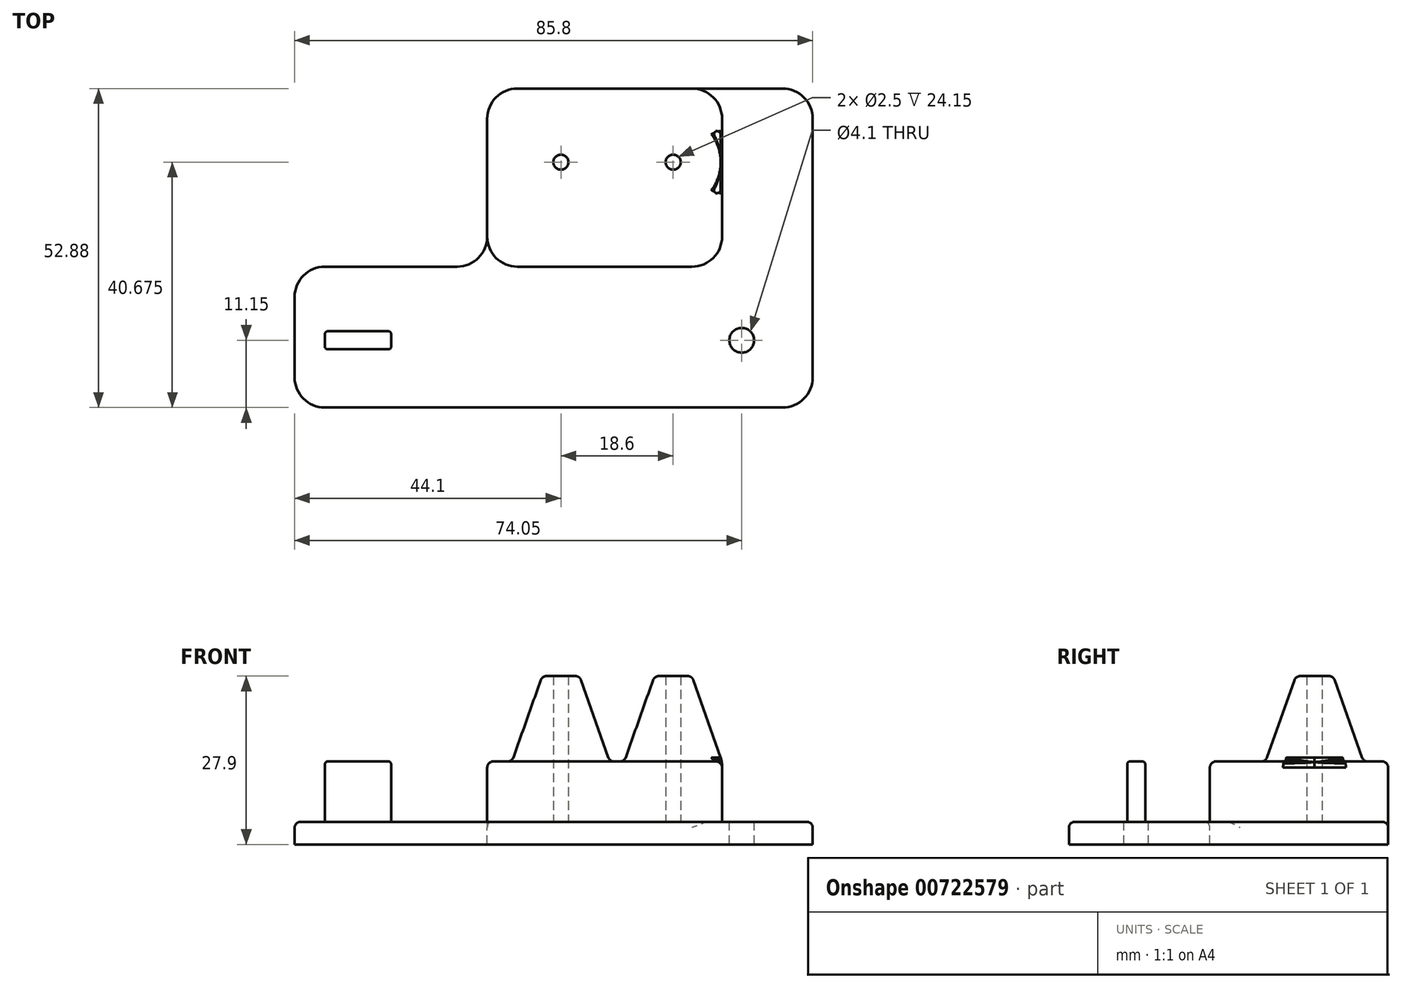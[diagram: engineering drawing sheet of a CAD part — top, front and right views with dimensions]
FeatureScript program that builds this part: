
annotation { "Feature Type Name" : "Feature", "Feature Type Description" : "" }
export const myFeature = defineFeature(function(context is Context, id is Id, definition is map)
    precondition{}
    {
        {
            var Q0;
            Q0=qCreatedBy(makeId("Top.planeOp"),FACE);
            var sketch = newSketch(context, id + "F0", { "sketchPlane" : qUnion([Q0])});
            skCircle(sketch, "E0", {"center": v(0, 0) * mm, "radius": 2.05 * mm});
            skLineSegment(sketch, "E1", {"start": v(2.05, 0) * mm, "end": v(40.45, 0) * mm, "construction": true});
            skLineSegment(sketch, "E2", {"start": v(40.45, 50) * mm, "end": v(40.45, 0) * mm, "construction": true});
            skCircle(sketch, "E3", {"center": v(-29.95, 29.52) * mm, "radius": 3.1 * mm});
            skCircle(sketch, "E4", {"center": v(-11.35, 29.52) * mm, "radius": 3.1 * mm});
            skLineSegment(sketch, "E5", {"start": v(-33.05, 30) * mm, "end": v(-33.05, 0) * mm, "construction": true});
            skLineSegment(sketch, "E6", {"start": v(-14.45, 30) * mm, "end": v(-14.45, 0) * mm, "construction": true});
            skLineSegment(sketch, "E7", {"start": v(-4.95, 0) * mm, "end": v(-4.95, 30) * mm, "construction": true});
            skLineSegment(sketch, "E8", {"start": v(-3.25, 41.72) * mm, "end": v(-3.25, 12.2) * mm});
            skLineSegment(sketch, "E9", {"start": v(0, -11.15) * mm, "end": v(-33.05, -11.15) * mm, "construction": true});
            skLineSegment(sketch, "E10", {"start": v(-29.95, 29.52) * mm, "end": v(-11.35, 29.52) * mm, "construction": true});
            skLineSegment(sketch, "E11", {"start": v(-29.95, 30.4) * mm, "end": v(-11.35, 30.4) * mm, "construction": true});
            skLineSegment(sketch, "E12", {"start": v(-3.25, 12.2) * mm, "end": v(-42.15, 12.2) * mm});
            skLineSegment(sketch, "E13", {"start": v(-42.15, 12.2) * mm, "end": v(-42.15, 41.72) * mm});
            skLineSegment(sketch, "E14", {"start": v(-42.15, 41.72) * mm, "end": v(-3.25, 41.72) * mm});
            skLineSegment(sketch, "E15", {"start": v(-3.25, 41.72) * mm, "end": v(11.75, 41.72) * mm});
            skLineSegment(sketch, "E16", {"start": v(11.75, 41.72) * mm, "end": v(11.75, -11.15) * mm});
            skLineSegment(sketch, "E17", {"start": v(11.75, -11.15) * mm, "end": v(-42.15, -11.15) * mm});
            skLineSegment(sketch, "E18", {"start": v(-42.15, -11.15) * mm, "end": v(-42.15, 12.2) * mm});
            skCircle(sketch, "E19", {"center": v(-11.35, 29.52) * mm, "radius": 1.25 * mm});
            skCircle(sketch, "E20", {"center": v(-29.95, 29.52) * mm, "radius": 1.25 * mm});
            skLineSegment(sketch, "E21.bottom", {"start": v(-69.05, 1.5) * mm, "end": v(-58.05, 1.5) * mm});
            skLineSegment(sketch, "E21.top", {"start": v(-69.05, -1.5) * mm, "end": v(-58.05, -1.5) * mm});
            skLineSegment(sketch, "E21.left", {"start": v(-69.05, 1.5) * mm, "end": v(-69.05, -1.5) * mm});
            skLineSegment(sketch, "E21.right", {"start": v(-58.05, 1.5) * mm, "end": v(-58.05, -1.5) * mm});
            skLineSegment(sketch, "E22", {"start": v(-69.05, -1.5) * mm, "end": v(-58.05, 1.5) * mm, "construction": true});
            skLineSegment(sketch, "E23", {"start": v(-63.55, 0) * mm, "end": v(-14.45, 0) * mm, "construction": true});
            skLineSegment(sketch, "E24", {"start": v(-42.15, 12.2) * mm, "end": v(-74.05, 12.2) * mm});
            skLineSegment(sketch, "E25", {"start": v(-74.05, 12.2) * mm, "end": v(-74.05, -11.15) * mm});
            skLineSegment(sketch, "E26", {"start": v(-74.05, -11.15) * mm, "end": v(-42.15, -11.15) * mm});
            skSolve(sketch);
        }
        {
            var Q0;
            Q0=makeQuery(id+"F0.imprint","IMPRINT",FACE,{"disambiguationData":[TD([[makeQuery(id+"F0.imprint","IMPRINT",EDGE,{"derivedFrom":sQuery(id+"F0.wireOp",EDGE,"E3")}),1.0]])]});
            var Q1;
            Q1=makeQuery(id+"F0.imprint","IMPRINT",FACE,{"disambiguationData":[TD([[makeQuery(id+"F0.imprint","IMPRINT",EDGE,{"derivedFrom":sQuery(id+"F0.wireOp",EDGE,"E4")}),1.0]])]});
            var Q2;
            Q2=makeQuery(id+"F0.imprint","IMPRINT",FACE,{"disambiguationData":[TD([[makeQuery(id+"F0.imprint","IMPRINT",EDGE,{"derivedFrom":sQuery(id+"F0.wireOp",EDGE,"E3")}),-1.0]])]});
            var Q3;
            Q3=makeQuery(id+"F0.imprint","IMPRINT",FACE,{"disambiguationData":[TD([[makeQuery(id+"F0.imprint","IMPRINT",EDGE,{"derivedFrom":sQuery(id+"F0.wireOp",EDGE,"E0")}),-1.0]])]});
            var Q4;
            Q4=makeQuery(id+"F0.imprint","IMPRINT",FACE,{"disambiguationData":[TD([[makeQuery(id+"F0.imprint","IMPRINT",EDGE,{"derivedFrom":sQuery(id+"F0.wireOp",EDGE,"E20")}),1.0]])]});
            var Q5;
            Q5=makeQuery(id+"F0.imprint","IMPRINT",FACE,{"disambiguationData":[TD([[makeQuery(id+"F0.imprint","IMPRINT",EDGE,{"derivedFrom":sQuery(id+"F0.wireOp",EDGE,"E19")}),1.0]])]});
            var Q6;
            Q6=makeQuery(id+"F0.imprint","IMPRINT",FACE,{"disambiguationData":[TD([[makeQuery(id+"F0.imprint","IMPRINT",EDGE,{"derivedFrom":sQuery(id+"F0.wireOp",EDGE,"E18")}),1.0]])]});
            var Q7;
            Q7=makeQuery(id+"F0.imprint","IMPRINT",FACE,{"disambiguationData":[TD([[makeQuery(id+"F0.imprint","IMPRINT",EDGE,{"derivedFrom":sQuery(id+"F0.wireOp",EDGE,"E21.bottom")}),-1.0]])]});
            extrude(context, id + "F1", {"entities" : qUnion([Q0, Q1, Q2, Q3, Q4, Q5, Q6, Q7]), "oppositeDirection" : true, "depth" : 3.75 * mm, "offsetDistance" : 25 * mm});
        }
        {
            var Q0;
            Q0=makeQuery(id+"F0.imprint","IMPRINT",FACE,{"disambiguationData":[TD([[makeQuery(id+"F0.imprint","IMPRINT",EDGE,{"derivedFrom":sQuery(id+"F0.wireOp",EDGE,"E3")}),1.0]])]});
            var Q1;
            Q1=makeQuery(id+"F0.imprint","IMPRINT",FACE,{"disambiguationData":[TD([[makeQuery(id+"F0.imprint","IMPRINT",EDGE,{"derivedFrom":sQuery(id+"F0.wireOp",EDGE,"E4")}),1.0]])]});
            var Q2;
            Q2=makeQuery(id+"F0.imprint","IMPRINT",FACE,{"disambiguationData":[TD([[makeQuery(id+"F0.imprint","IMPRINT",EDGE,{"derivedFrom":sQuery(id+"F0.wireOp",EDGE,"E3")}),-1.0]])]});
            var Q3;
            Q3=makeQuery(id+"F0.imprint","IMPRINT",FACE,{"disambiguationData":[TD([[makeQuery(id+"F0.imprint","IMPRINT",EDGE,{"derivedFrom":sQuery(id+"F0.wireOp",EDGE,"E21.bottom")}),-1.0]])]});
            extrude(context, id + "F2", {"entities" : qUnion([Q0, Q1, Q2, Q3]), "operationType" : NewBodyOperationType.ADD, "depth" : 10 * mm, "offsetDistance" : 25 * mm});
        }
        {
            var Q0;
            Q0=makeQuery(id+"F0.imprint","IMPRINT",FACE,{"disambiguationData":[TD([[makeQuery(id+"F0.imprint","IMPRINT",EDGE,{"derivedFrom":sQuery(id+"F0.wireOp",EDGE,"E4")}),1.0]])]});
            var Q1;
            Q1=makeQuery(id+"F0.imprint","IMPRINT",FACE,{"disambiguationData":[TD([[makeQuery(id+"F0.imprint","IMPRINT",EDGE,{"derivedFrom":sQuery(id+"F0.wireOp",EDGE,"E3")}),1.0]])]});
            extrude(context, id + "F3", {"entities" : qUnion([Q0, Q1]), "operationType" : NewBodyOperationType.ADD, "depth" : 24.15 * mm, "offsetDistance" : 25 * mm});
        }
        {
            var Q0;
            Q0=makeQuery(id+"F3.boolean.opBoolean","INTERSECT",EDGE,{"derivedFrom":[makeQuery(id+"F2.opExtrude","CAP_FACE",FACE,{"disambiguationData":[OSD([sQuery(id+"F0.wireOp",EDGE,"E8"),sQuery(id+"F0.wireOp",EDGE,"E12"),sQuery(id+"F0.wireOp",EDGE,"E13"),sQuery(id+"F0.wireOp",EDGE,"E14"),sQuery(id+"F0.wireOp",EDGE,"E19"),sQuery(id+"F0.wireOp",EDGE,"E20")])],"isStart":false}),makeQuery(id+"F3.opExtrude","SWEPT_FACE",FACE,{"disambiguationData":[OSD([sQuery(id+"F0.wireOp",EDGE,"E3")])]})]});
            var Q1;
            Q1=makeQuery(id+"F3.boolean.opBoolean","INTERSECT",EDGE,{"derivedFrom":[makeQuery(id+"F2.opExtrude","CAP_FACE",FACE,{"disambiguationData":[OSD([sQuery(id+"F0.wireOp",EDGE,"E8"),sQuery(id+"F0.wireOp",EDGE,"E12"),sQuery(id+"F0.wireOp",EDGE,"E13"),sQuery(id+"F0.wireOp",EDGE,"E14"),sQuery(id+"F0.wireOp",EDGE,"E19"),sQuery(id+"F0.wireOp",EDGE,"E20")])],"isStart":false}),makeQuery(id+"F3.opExtrude","SWEPT_FACE",FACE,{"disambiguationData":[OSD([sQuery(id+"F0.wireOp",EDGE,"E4")])]})]});
            chamfer(context, id + "F4", {"entities" : qUnion([Q0, Q1]), "chamferType" : ChamferType.TWO_OFFSETS, "width1" : 5 * mm, "oppositeDirection" : false, "width2" : 14.15 * mm, "tangentPropagation" : true});
        }
        {
            var Q0;
            Q0=makeQuery(id+"F1.opExtrude","SWEPT_EDGE",EDGE,{"disambiguationData":[OSD([sQuery(id+"F0.wireOp",EDGE,"E16"),sQuery(id+"F0.wireOp",EDGE,"E17")])]});
            var Q1;
            Q1=makeQuery(id+"F1.opExtrude","SWEPT_EDGE",EDGE,{"disambiguationData":[OSD([sQuery(id+"F0.wireOp",EDGE,"E17"),sQuery(id+"F0.wireOp",EDGE,"E18")])]});
            var Q2;
            Q2=makeQuery(id+"F1.opExtrude","SWEPT_EDGE",EDGE,{"disambiguationData":[OSD([sQuery(id+"F0.wireOp",EDGE,"E15"),sQuery(id+"F0.wireOp",EDGE,"E16")])]});
            var Q3;
            Q3=makeQuery(id+"F2.opExtrude","SWEPT_EDGE",EDGE,{"disambiguationData":[OSD([sQuery(id+"F0.wireOp",EDGE,"E8"),sQuery(id+"F0.wireOp",EDGE,"E12")])]});
            var Q4;
            Q4=makeQuery(id+"F2.opExtrude","SWEPT_EDGE",EDGE,{"disambiguationData":[OSD([sQuery(id+"F0.wireOp",EDGE,"E12"),sQuery(id+"F0.wireOp",EDGE,"E13"),sQuery(id+"F0.wireOp",EDGE,"E18")])]});
            var Q5;
            {var subQ0=sQuery(id+"F0.wireOp",EDGE,"E14");var subQ1=sQuery(id+"F0.wireOp",EDGE,"E13");Q5=makeQuery(id+"F2.boolean.opBoolean","MERGE",EDGE,{"derivedFrom":[makeQuery(id+"F1.opExtrude","SWEPT_EDGE",EDGE,{"disambiguationData":[OSD([subQ1,subQ0])]}),makeQuery(id+"F2.opExtrude","SWEPT_EDGE",EDGE,{"disambiguationData":[OSD([subQ1,subQ0])]})]});}
            var Q6;
            Q6=makeQuery(id+"F2.opExtrude","SWEPT_EDGE",EDGE,{"disambiguationData":[OSD([sQuery(id+"F0.wireOp",EDGE,"E8"),sQuery(id+"F0.wireOp",EDGE,"E14"),sQuery(id+"F0.wireOp",EDGE,"E15")])]});
            var Q7;
            Q7=makeQuery(id+"F1.opExtrude","SWEPT_EDGE",EDGE,{"disambiguationData":[OSD([sQuery(id+"F0.wireOp",EDGE,"E24"),sQuery(id+"F0.wireOp",EDGE,"E25")])]});
            var Q8;
            Q8=makeQuery(id+"F1.opExtrude","SWEPT_EDGE",EDGE,{"disambiguationData":[OSD([sQuery(id+"F0.wireOp",EDGE,"E25"),sQuery(id+"F0.wireOp",EDGE,"E26")])]});
            fillet(context, id + "F5", {"entities" : qUnion([Q0, Q1, Q2, Q3, Q4, Q5, Q6, Q7, Q8]), "radius" : 5 * mm, "tangentPropagation" : true, "allowEdgeOverflow" : false});
        }
        {
            var Q0;
            Q0=makeQuery(id+"F1.opExtrude","SWEPT_EDGE",EDGE,{"disambiguationData":[OSD([sQuery(id+"F0.wireOp",EDGE,"E12"),sQuery(id+"F0.wireOp",EDGE,"E13"),sQuery(id+"F0.wireOp",EDGE,"E18"),sQuery(id+"F0.wireOp",EDGE,"E24")])]});
            fillet(context, id + "F6", {"entities" : qUnion([Q0]), "radius" : 5 * mm, "tangentPropagation" : true, "allowEdgeOverflow" : false});
        }
        {
            var Q0;
            Q0=makeQuery(id+"F2.opExtrude","CAP_FACE",FACE,{"disambiguationData":[OSD([sQuery(id+"F0.wireOp",EDGE,"E21.bottom"),sQuery(id+"F0.wireOp",EDGE,"E21.top"),sQuery(id+"F0.wireOp",EDGE,"E21.left"),sQuery(id+"F0.wireOp",EDGE,"E21.right")])],"isStart":false});
            var Q1;
            Q1=makeQuery(id+"F2.opExtrude","SWEPT_EDGE",EDGE,{"disambiguationData":[OSD([sQuery(id+"F0.wireOp",EDGE,"E21.bottom"),sQuery(id+"F0.wireOp",EDGE,"E21.left")])]});
            var Q2;
            Q2=makeQuery(id+"F2.opExtrude","SWEPT_EDGE",EDGE,{"disambiguationData":[OSD([sQuery(id+"F0.wireOp",EDGE,"E21.top"),sQuery(id+"F0.wireOp",EDGE,"E21.left")])]});
            var Q3;
            Q3=makeQuery(id+"F2.opExtrude","SWEPT_EDGE",EDGE,{"disambiguationData":[OSD([sQuery(id+"F0.wireOp",EDGE,"E21.bottom"),sQuery(id+"F0.wireOp",EDGE,"E21.right")])]});
            var Q4;
            Q4=makeQuery(id+"F2.opExtrude","SWEPT_EDGE",EDGE,{"disambiguationData":[OSD([sQuery(id+"F0.wireOp",EDGE,"E21.top"),sQuery(id+"F0.wireOp",EDGE,"E21.right")])]});
            fillet(context, id + "F7", {"entities" : qUnion([Q0, Q1, Q2, Q3, Q4]), "radius" : 0.5 * mm, "tangentPropagation" : true, "allowEdgeOverflow" : false});
        }
        {
            var Q0;
            Q0=makeQuery(id+"F2.opExtrude","CAP_FACE",FACE,{"disambiguationData":[OSD([sQuery(id+"F0.wireOp",EDGE,"E8"),sQuery(id+"F0.wireOp",EDGE,"E12"),sQuery(id+"F0.wireOp",EDGE,"E13"),sQuery(id+"F0.wireOp",EDGE,"E14"),sQuery(id+"F0.wireOp",EDGE,"E19"),sQuery(id+"F0.wireOp",EDGE,"E20")])],"isStart":false});
            var Q1;
            {var subQ0=sQuery(id+"F0.wireOp",EDGE,"E20");var subQ1=sQuery(id+"F0.wireOp",EDGE,"E3");Q1=makeQuery(id+"F4.opChamfer","BLEND_EDGE",EDGE,{"blendedFrom":[makeQuery(id+"F3.boolean.opBoolean","INTERSECT",EDGE,{"derivedFrom":[makeQuery(id+"F2.opExtrude","CAP_FACE",FACE,{"disambiguationData":[OSD([sQuery(id+"F0.wireOp",EDGE,"E8"),sQuery(id+"F0.wireOp",EDGE,"E12"),sQuery(id+"F0.wireOp",EDGE,"E13"),sQuery(id+"F0.wireOp",EDGE,"E14"),sQuery(id+"F0.wireOp",EDGE,"E19"),subQ0])],"isStart":false}),makeQuery(id+"F3.opExtrude","SWEPT_FACE",FACE,{"disambiguationData":[OSD([subQ1])]})]}),makeQuery(id+"F3.opExtrude","CAP_FACE",FACE,{"disambiguationData":[OSD([subQ1,subQ0])],"isStart":false})],"blendedInto":[makeQuery(id+"F3.opExtrude","CAP_FACE",FACE,{"disambiguationData":[OSD([subQ1,subQ0])],"isStart":false})]});}
            var Q2;
            {var subQ0=sQuery(id+"F0.wireOp",EDGE,"E19");var subQ1=sQuery(id+"F0.wireOp",EDGE,"E4");Q2=makeQuery(id+"F4.opChamfer","BLEND_EDGE",EDGE,{"blendedFrom":[makeQuery(id+"F3.boolean.opBoolean","INTERSECT",EDGE,{"derivedFrom":[makeQuery(id+"F2.opExtrude","CAP_FACE",FACE,{"disambiguationData":[OSD([sQuery(id+"F0.wireOp",EDGE,"E8"),sQuery(id+"F0.wireOp",EDGE,"E12"),sQuery(id+"F0.wireOp",EDGE,"E13"),sQuery(id+"F0.wireOp",EDGE,"E14"),subQ0,sQuery(id+"F0.wireOp",EDGE,"E20")])],"isStart":false}),makeQuery(id+"F3.opExtrude","SWEPT_FACE",FACE,{"disambiguationData":[OSD([subQ1])]})]}),makeQuery(id+"F3.opExtrude","CAP_FACE",FACE,{"disambiguationData":[OSD([subQ1,subQ0])],"isStart":false})],"blendedInto":[makeQuery(id+"F3.opExtrude","CAP_FACE",FACE,{"disambiguationData":[OSD([subQ1,subQ0])],"isStart":false})]});}
            var Q3;
            Q3=makeQuery(id+"F1.opExtrude","CAP_EDGE",EDGE,{"disambiguationData":[OSD([sQuery(id+"F0.wireOp",EDGE,"E17"),sQuery(id+"F0.wireOp",EDGE,"E26")])],"isStart":true});
            fillet(context, id + "F8", {"entities" : qUnion([Q0, Q1, Q2, Q3]), "radius" : 1 * mm, "tangentPropagation" : true, "allowEdgeOverflow" : false});
        }
    });
